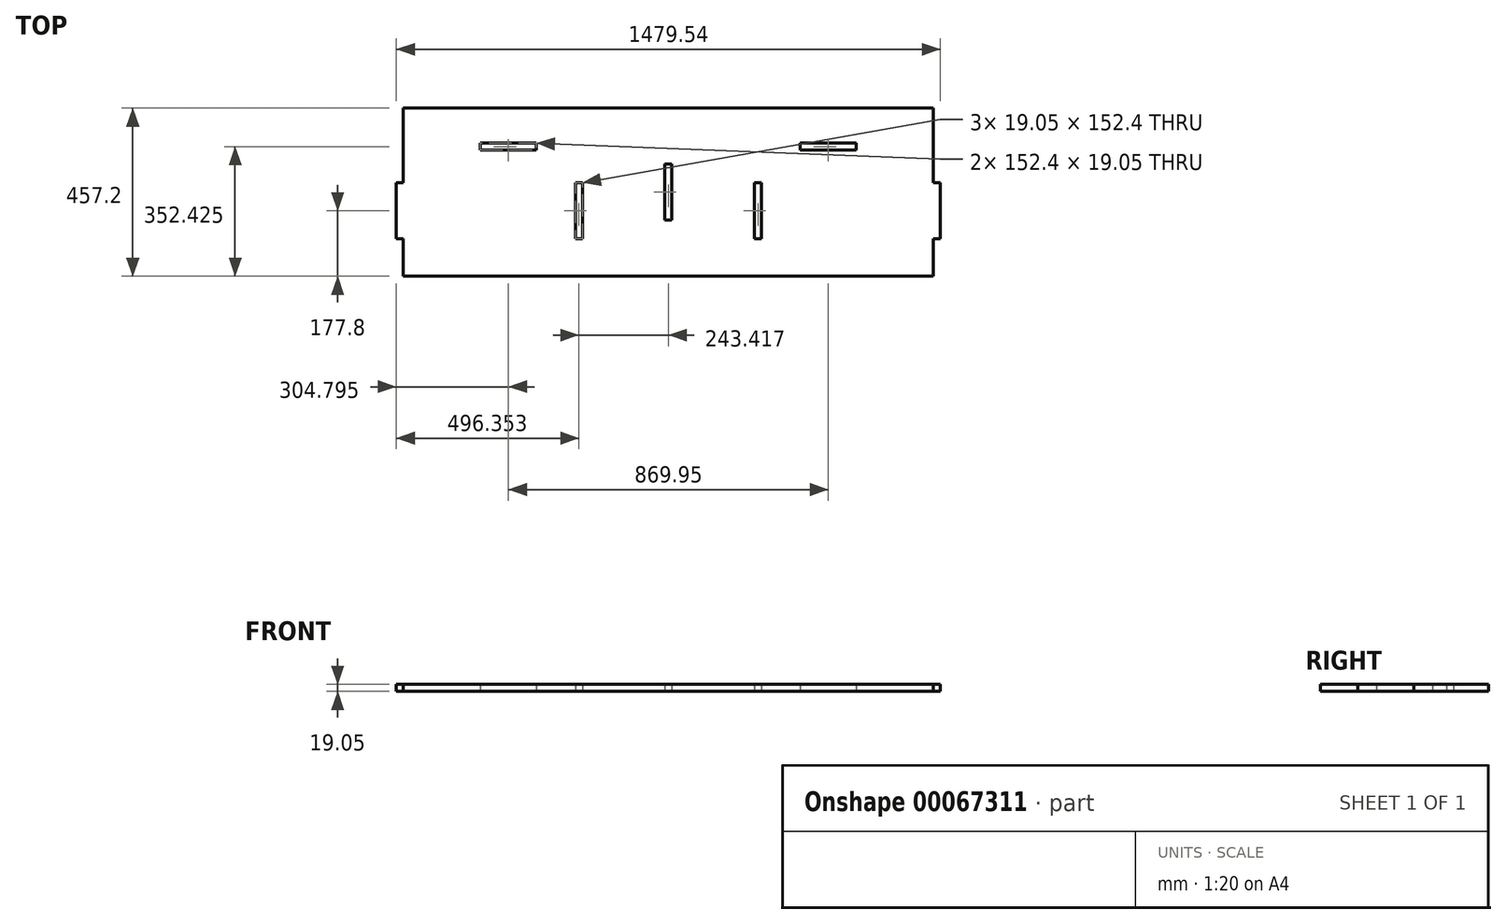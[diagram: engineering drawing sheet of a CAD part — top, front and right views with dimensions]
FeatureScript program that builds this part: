
annotation { "Feature Type Name" : "Feature", "Feature Type Description" : "" }
export const myFeature = defineFeature(function(context is Context, id is Id, definition is map)
    precondition{}
    {
        {
            var Q0;
            Q0=qCreatedBy(makeId("Top.planeOp"),FACE);
            var sketch = newSketch(context, id + "F0", { "sketchPlane" : qUnion([Q0])});
            skLineSegment(sketch, "E0.bottom", {"start": v(-720.73, 0) * mm, "end": v(720.73, 0) * mm});
            skLineSegment(sketch, "E0.top", {"start": v(-720.73, -457.2) * mm, "end": v(720.73, -457.2) * mm});
            skLineSegment(sketch, "E0.left", {"start": v(-720.73, 0) * mm, "end": v(-720.73, -457.2) * mm});
            skLineSegment(sketch, "E0.right", {"start": v(720.73, 0) * mm, "end": v(720.73, -457.2) * mm});
            skLineSegment(sketch, "E1.bottom", {"start": v(-720.73, -355.6) * mm, "end": v(-739.78, -355.6) * mm});
            skLineSegment(sketch, "E1.top", {"start": v(-720.73, -203.2) * mm, "end": v(-739.78, -203.2) * mm});
            skLineSegment(sketch, "E1.left", {"start": v(-720.73, -355.6) * mm, "end": v(-720.73, -203.2) * mm});
            skLineSegment(sketch, "E1.right", {"start": v(-739.78, -355.6) * mm, "end": v(-739.78, -203.2) * mm});
            skLineSegment(sketch, "E2.bottom", {"start": v(-441.33, 0) * mm, "end": v(-288.93, 0) * mm});
            skLineSegment(sketch, "E2.top", {"start": v(-441.33, 19.05) * mm, "end": v(-288.93, 19.05) * mm});
            skLineSegment(sketch, "E2.left", {"start": v(-441.33, 0) * mm, "end": v(-441.33, 19.05) * mm});
            skLineSegment(sketch, "E2.right", {"start": v(-288.93, 0) * mm, "end": v(-288.93, 19.05) * mm});
            skLineSegment(sketch, "E3.bottom", {"start": v(288.93, 0) * mm, "end": v(441.33, 0) * mm});
            skLineSegment(sketch, "E3.top", {"start": v(288.93, 19.05) * mm, "end": v(441.33, 19.05) * mm});
            skLineSegment(sketch, "E3.left", {"start": v(288.93, 0) * mm, "end": v(288.93, 19.05) * mm});
            skLineSegment(sketch, "E3.right", {"start": v(441.33, 0) * mm, "end": v(441.33, 19.05) * mm});
            skLineSegment(sketch, "E4.bottom", {"start": v(720.73, -203.2) * mm, "end": v(739.78, -203.2) * mm});
            skLineSegment(sketch, "E4.top", {"start": v(720.73, -355.6) * mm, "end": v(739.77, -355.6) * mm});
            skLineSegment(sketch, "E4.left", {"start": v(720.73, -203.2) * mm, "end": v(720.73, -355.6) * mm});
            skLineSegment(sketch, "E4.right", {"start": v(739.77, -203.2) * mm, "end": v(739.77, -355.6) * mm});
            skLineSegment(sketch, "E5.bottom", {"start": v(-9.53, -152.4) * mm, "end": v(9.52, -152.4) * mm});
            skLineSegment(sketch, "E5.top", {"start": v(-9.53, -304.8) * mm, "end": v(9.52, -304.8) * mm});
            skLineSegment(sketch, "E5.left", {"start": v(-9.53, -152.4) * mm, "end": v(-9.53, -304.8) * mm});
            skLineSegment(sketch, "E5.right", {"start": v(9.52, -152.4) * mm, "end": v(9.52, -304.8) * mm});
            skLineSegment(sketch, "E6.bottom", {"start": v(-252.94, -203.2) * mm, "end": v(-233.9, -203.2) * mm});
            skLineSegment(sketch, "E6.top", {"start": v(-252.94, -355.6) * mm, "end": v(-233.9, -355.6) * mm});
            skLineSegment(sketch, "E6.left", {"start": v(-252.94, -203.2) * mm, "end": v(-252.94, -355.6) * mm});
            skLineSegment(sketch, "E6.right", {"start": v(-233.9, -203.2) * mm, "end": v(-233.9, -355.6) * mm});
            skLineSegment(sketch, "E7.bottom", {"start": v(233.9, -203.2) * mm, "end": v(252.94, -203.2) * mm});
            skLineSegment(sketch, "E7.top", {"start": v(233.9, -355.6) * mm, "end": v(252.94, -355.6) * mm});
            skLineSegment(sketch, "E7.left", {"start": v(233.9, -203.2) * mm, "end": v(233.9, -355.6) * mm});
            skLineSegment(sketch, "E7.right", {"start": v(252.94, -203.2) * mm, "end": v(252.94, -355.6) * mm});
            skLineSegment(sketch, "E8.bottom", {"start": v(-511.18, -95.25) * mm, "end": v(-358.78, -95.25) * mm});
            skLineSegment(sketch, "E8.top", {"start": v(-511.18, -114.3) * mm, "end": v(-358.78, -114.3) * mm});
            skLineSegment(sketch, "E8.left", {"start": v(-511.18, -95.25) * mm, "end": v(-511.18, -114.3) * mm});
            skLineSegment(sketch, "E8.right", {"start": v(-358.78, -95.25) * mm, "end": v(-358.78, -114.3) * mm});
            skPoint(sketch, "E9.firstSnap0", {"position": v(233.9, -279.4) * mm});
            skLineSegment(sketch, "E10.bottom", {"start": v(358.78, -95.25) * mm, "end": v(511.17, -95.25) * mm});
            skLineSegment(sketch, "E10.top", {"start": v(358.78, -114.3) * mm, "end": v(511.18, -114.3) * mm});
            skLineSegment(sketch, "E10.left", {"start": v(358.78, -95.25) * mm, "end": v(358.78, -114.3) * mm});
            skLineSegment(sketch, "E10.right", {"start": v(511.17, -95.25) * mm, "end": v(511.17, -114.3) * mm});
            skSolve(sketch);
        }
        {
            var Q0;
            Q0=makeQuery(id+"F0.imprint","IMPRINT",FACE,{"disambiguationData":[TD([[makeQuery(id+"F0.imprint","IMPRINT",EDGE,{"derivedFrom":sQuery(id+"F0.wireOp",EDGE,"E0.bottom")}),-1.0]])]});
            var Q1;
            Q1=makeQuery(id+"F0.imprint","IMPRINT",FACE,{"disambiguationData":[TD([[makeQuery(id+"F0.imprint","IMPRINT",EDGE,{"derivedFrom":sQuery(id+"F0.wireOp",EDGE,"E2.bottom")}),1.0]])]});
            var Q2;
            Q2=makeQuery(id+"F0.imprint","IMPRINT",FACE,{"disambiguationData":[TD([[makeQuery(id+"F0.imprint","IMPRINT",EDGE,{"derivedFrom":sQuery(id+"F0.wireOp",EDGE,"E3.bottom")}),1.0]])]});
            var Q3;
            Q3=makeQuery(id+"F0.imprint","IMPRINT",FACE,{"disambiguationData":[TD([[makeQuery(id+"F0.imprint","IMPRINT",EDGE,{"derivedFrom":sQuery(id+"F0.wireOp",EDGE,"E4.bottom")}),-1.0]])]});
            var Q4;
            Q4=makeQuery(id+"F0.imprint","IMPRINT",FACE,{"disambiguationData":[TD([[makeQuery(id+"F0.imprint","IMPRINT",EDGE,{"derivedFrom":sQuery(id+"F0.wireOp",EDGE,"E1.bottom")}),-1.0]])]});
            extrude(context, id + "F1", {"entities" : qUnion([Q0, Q1, Q2, Q3, Q4]), "depth" : 19.05 * mm});
        }
    });
